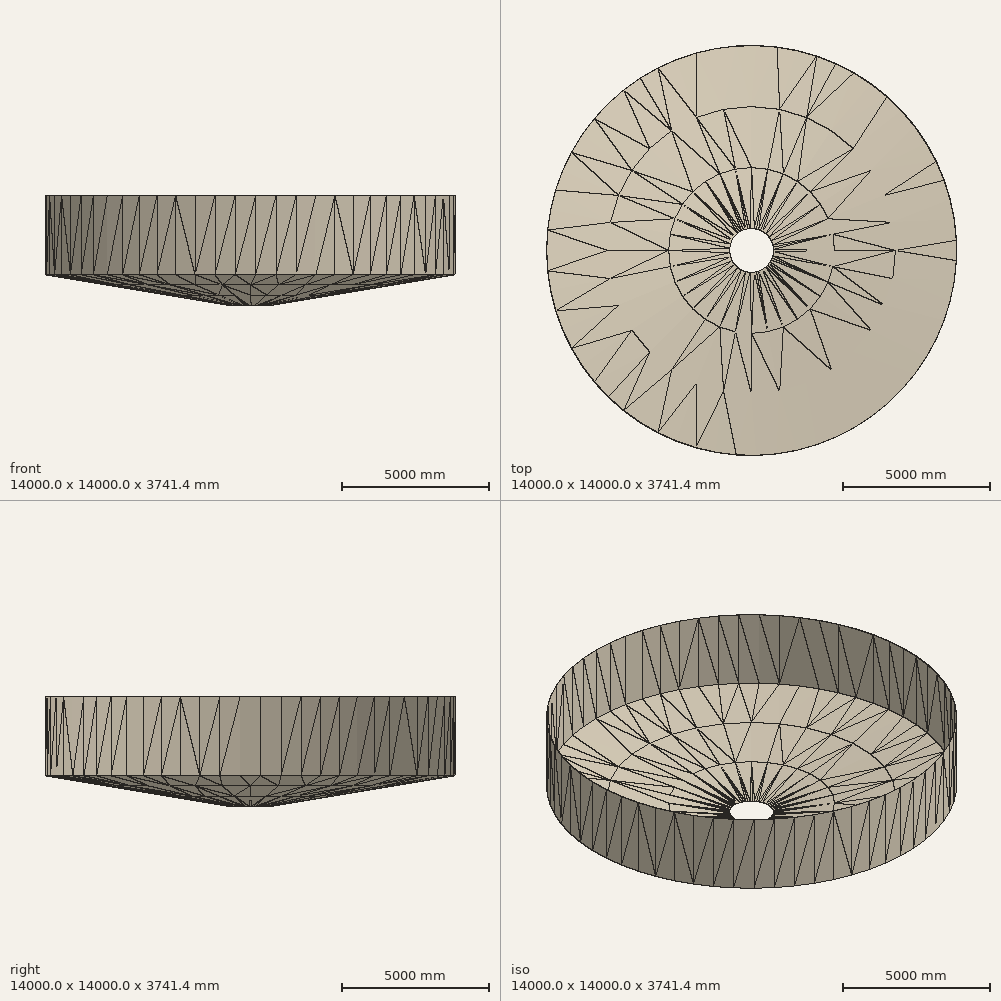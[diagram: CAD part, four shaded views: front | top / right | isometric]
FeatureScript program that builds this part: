
annotation { "Feature Type Name" : "Feature", "Feature Type Description" : "" }
export const myFeature = defineFeature(function(context is Context, id is Id, definition is map)
    precondition{}
    {
        {
            var Q0;
            Q0=qCreatedBy(makeId("Front.planeOp"),FACE);
            var sketch = newSketch(context, id + "F0", { "sketchPlane" : qUnion([Q0])});
            skLineSegment(sketch, "E0", {"start": v(-7000, 3038) * mm, "end": v(-750, 1996.6) * mm});
            skLineSegment(sketch, "E1", {"start": v(-7000, 3038) * mm, "end": v(-7000, 2388.73) * mm, "construction": true});
            skLineSegment(sketch, "E2", {"start": v(-7000, 3038) * mm, "end": v(-7000, 5738) * mm});
            skLineSegment(sketch, "E3.0", {"start": v(-6993.65, 3043.38) * mm, "end": v(-6993.65, 5738) * mm});
            skLineSegment(sketch, "E3.1", {"start": v(-6993.65, 3043.38) * mm, "end": v(-748.96, 2002.86) * mm});
            skLineSegment(sketch, "E4", {"start": v(-7000, 5738) * mm, "end": v(-6993.65, 5738) * mm});
            skLineSegment(sketch, "E5", {"start": v(-750, 1996.6) * mm, "end": v(-748.96, 2002.86) * mm});
            skLineSegment(sketch, "E6", {"start": v(0, 0) * mm, "end": v(0, 3094.1) * mm, "construction": true});
            skSolve(sketch);
        }
        {
            var Q0;
            Q0=makeQuery(id+"F0.imprint","IMPRINT",FACE,{"disambiguationData":[TD([[makeQuery(id+"F0.imprint","IMPRINT",EDGE,{"derivedFrom":sQuery(id+"F0.wireOp",EDGE,"E0")}),1.0]])]});
            var Q1;
            Q1=sQuery(id+"F0.wireOp",EDGE,"E6");
            revolve(context, id + "F1", {"entities" : qUnion([Q0]), "axis" : qUnion([Q1]), "revolveType" : RevolveType.FULL});
        }
    });
